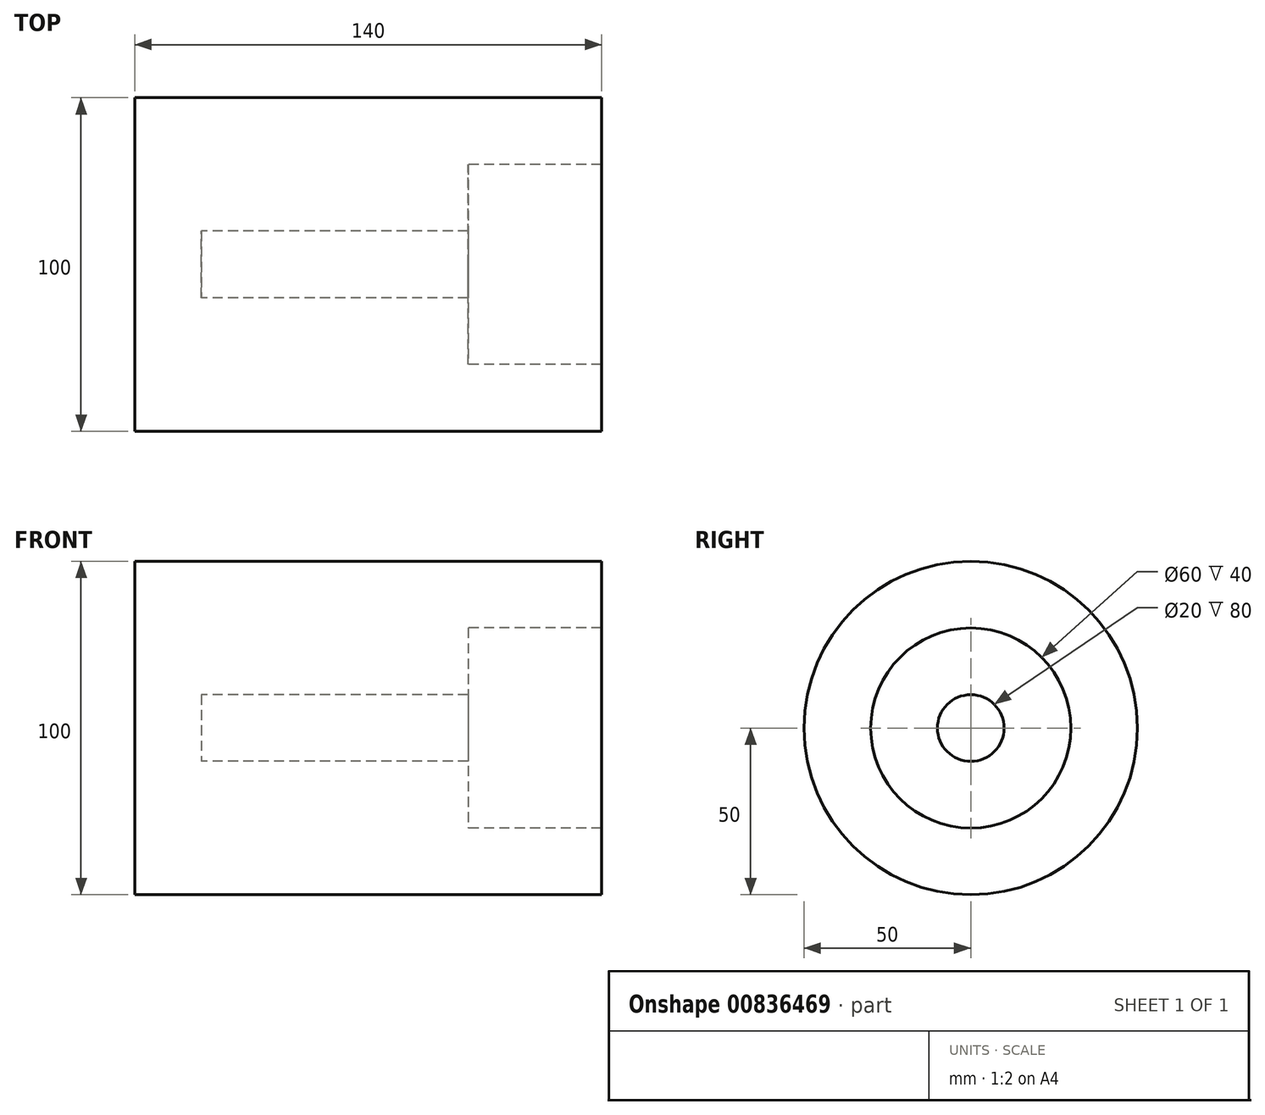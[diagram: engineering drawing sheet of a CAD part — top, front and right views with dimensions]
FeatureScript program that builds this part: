
annotation { "Feature Type Name" : "Feature", "Feature Type Description" : "" }
export const myFeature = defineFeature(function(context is Context, id is Id, definition is map)
    precondition{}
    {
        {
            var Q0;
            Q0=qCreatedBy(makeId("Front.planeOp"),FACE);
            var sketch = newSketch(context, id + "F0", { "sketchPlane" : qUnion([Q0])});
            skLineSegment(sketch, "E0.top", {"start": v(0, 100) * mm, "end": v(140, 100) * mm});
            skLineSegment(sketch, "E1.bottom", {"start": v(140, 80) * mm, "end": v(100, 80) * mm});
            skLineSegment(sketch, "E1.right", {"start": v(100, 80) * mm, "end": v(100, 60) * mm});
            skLineSegment(sketch, "E2.top", {"start": v(100, 60) * mm, "end": v(20, 60) * mm});
            skLineSegment(sketch, "E3.trimOffspring", {"start": v(140, 80) * mm, "end": v(140, 100) * mm});
            skLineSegment(sketch, "E4", {"start": v(0, 50) * mm, "end": v(20, 50) * mm});
            skLineSegment(sketch, "E5", {"start": v(20, 50) * mm, "end": v(20, 60) * mm});
            skLineSegment(sketch, "E6", {"start": v(0, 50) * mm, "end": v(0, 100) * mm});
            skLineSegment(sketch, "E7", {"start": v(-14.33, 50) * mm, "end": v(141.1, 50) * mm, "construction": true});
            skSolve(sketch);
        }
        {
            var Q0;
            Q0=makeQuery(id+"F0.imprint","IMPRINT",FACE,{"disambiguationData":[TD([[makeQuery(id+"F0.imprint","IMPRINT",EDGE,{"derivedFrom":sQuery(id+"F0.wireOp",EDGE,"E0.top")}),-1.0]])]});
            var Q1;
            Q1=sQuery(id+"F0.wireOp",EDGE,"E7");
            revolve(context, id + "F1", {"surfaceOperationType" : NewSurfaceOperationType.NEW, "entities" : qUnion([Q0]), "axis" : qUnion([Q1]), "revolveType" : RevolveType.FULL});
        }
    });
